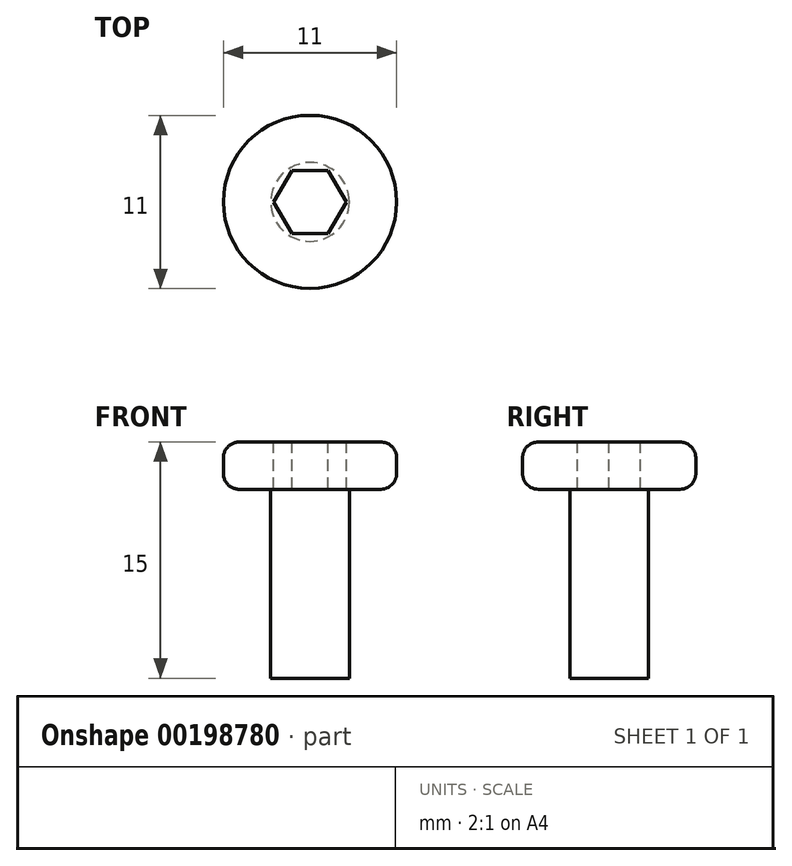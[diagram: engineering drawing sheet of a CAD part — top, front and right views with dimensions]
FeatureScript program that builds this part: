
annotation { "Feature Type Name" : "Feature", "Feature Type Description" : "" }
export const myFeature = defineFeature(function(context is Context, id is Id, definition is map)
    precondition{}
    {
        {
            var Q0;
            Q0=qCreatedBy(makeId("Front.planeOp"),FACE);
            var sketch = newSketch(context, id + "F0", { "sketchPlane" : qUnion([Q0])});
            skLineSegment(sketch, "E0", {"start": v(0, 0) * mm, "end": v(0, 15) * mm});
            skLineSegment(sketch, "E1", {"start": v(0, 15) * mm, "end": v(-4.5, 15) * mm});
            skLineSegment(sketch, "E2", {"start": v(-5.5, 14) * mm, "end": v(-5.5, 13) * mm});
            skLineSegment(sketch, "E3", {"start": v(-4.5, 12) * mm, "end": v(-2.5, 12) * mm});
            skLineSegment(sketch, "E4", {"start": v(-2.5, 12) * mm, "end": v(-2.5, 0) * mm});
            skLineSegment(sketch, "E5", {"start": v(-2.5, 0) * mm, "end": v(0, 0) * mm});
            skPoint(sketch, "E6.visualSharp", {"position": v(-5.5, 15) * mm});
            skArc(sketch, "E6.filletArc", {"start": v(-4.5, 15) * mm, "mid": v(-5.2, 14.7) * mm, "end": v(-5.5, 14) * mm});
            skPoint(sketch, "E7.visualSharp", {"position": v(-5.5, 12) * mm});
            skArc(sketch, "E7.filletArc", {"start": v(-5.5, 13) * mm, "mid": v(-5.2, 12.3) * mm, "end": v(-4.5, 12) * mm});
            skSolve(sketch);
        }
        {
            var Q0;
            Q0 = qSketchRegion(id + "F0", true);
            var Q1;
            Q1=sQuery(id+"F0.wireOp",EDGE,"E0");
            revolve(context, id + "F1", {"entities" : qUnion([Q0]), "axis" : qUnion([Q1]), "revolveType" : RevolveType.FULL});
        }
        {
            var Q0;
            Q0=makeQuery(id+"F1.opRevolve","SWEPT_FACE",FACE,{"disambiguationData":[OSD([sQuery(id+"F0.wireOp",EDGE,"E1")])]});
            var sketch = newSketch(context, id + "F2", { "sketchPlane" : qUnion([Q0])});
            skCircle(sketch, "E8.cCircle", {"center": v(0, 0) * mm, "radius": 2 * mm, "construction": true});
            skLineSegment(sketch, "E8.0", {"start": v(-1.15, 2) * mm, "end": v(1.15, 2) * mm});
            skLineSegment(sketch, "E8.1", {"start": v(1.15, 2) * mm, "end": v(2.3, 0) * mm});
            skLineSegment(sketch, "E8.2", {"start": v(2.3, 0) * mm, "end": v(1.15, -2) * mm});
            skLineSegment(sketch, "E8.3", {"start": v(1.15, -2) * mm, "end": v(-1.15, -2) * mm});
            skLineSegment(sketch, "E8.4", {"start": v(-1.15, -2) * mm, "end": v(-2.3, 0) * mm});
            skLineSegment(sketch, "E8.5", {"start": v(-2.3, 0) * mm, "end": v(-1.15, 2) * mm});
            skPoint(sketch, "E8.0.midPoint", {"position": v(0, 2) * mm});
            skSolve(sketch);
        }
        {
            var Q0;
            Q0 = qSketchRegion(id + "F2", true);
            extrude(context, id + "F3", {"entities" : qUnion([Q0]), "operationType" : NewBodyOperationType.REMOVE, "oppositeDirection" : true, "depth" : 3 * mm});
        }
    });
